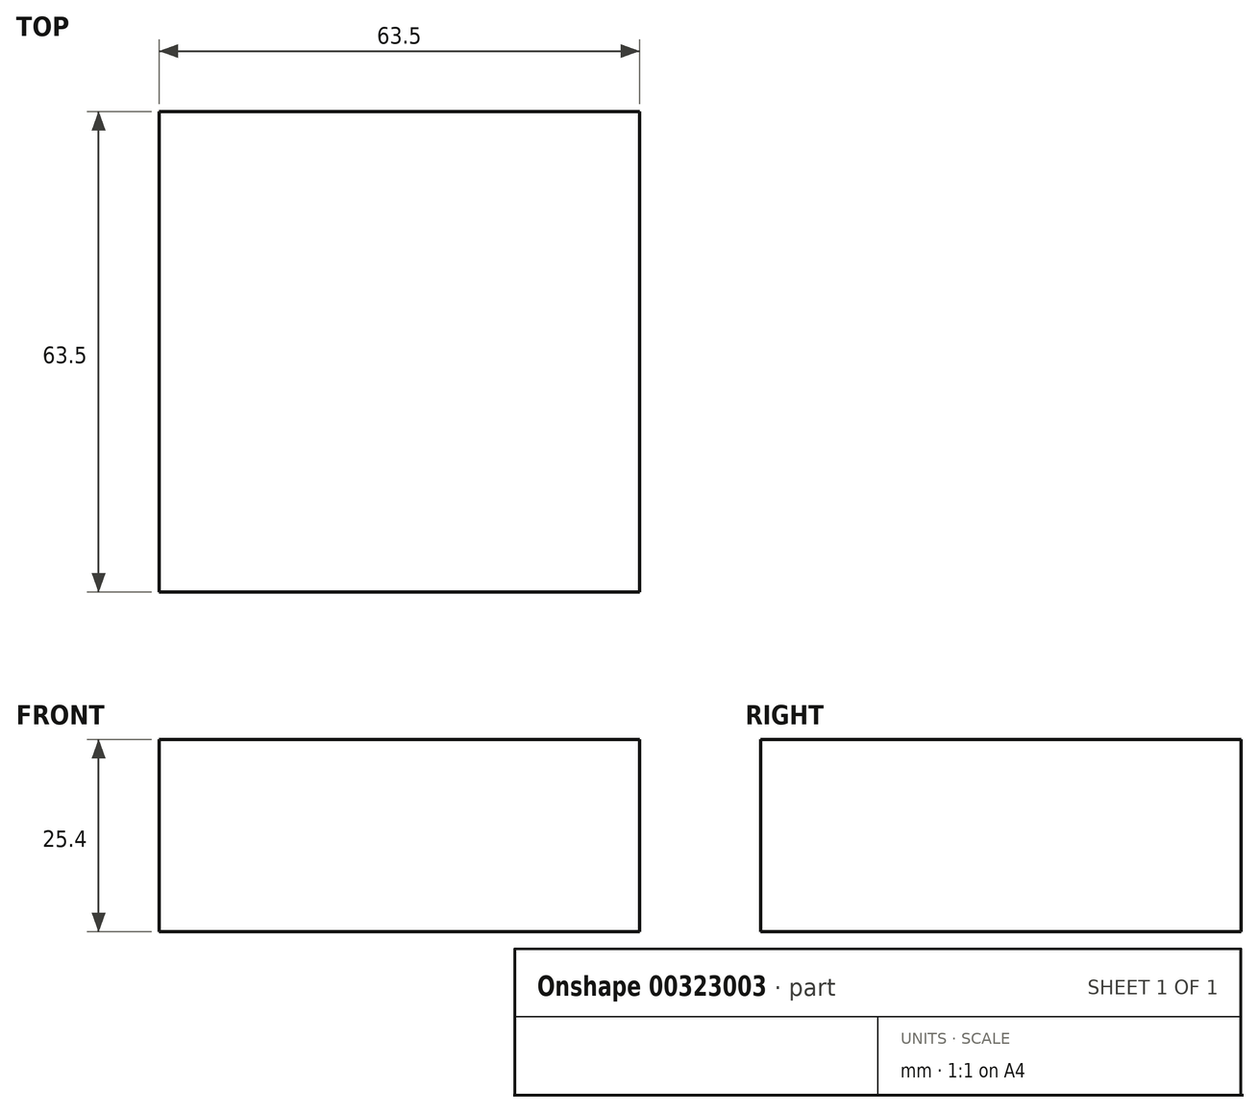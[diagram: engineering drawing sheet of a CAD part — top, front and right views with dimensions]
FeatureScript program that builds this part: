
annotation { "Feature Type Name" : "Feature", "Feature Type Description" : "" }
export const myFeature = defineFeature(function(context is Context, id is Id, definition is map)
    precondition{}
    {
        {
            var Q0;
            Q0=qCreatedBy(makeId("Top.planeOp"),FACE);
            var sketch = newSketch(context, id + "F0", { "sketchPlane" : qUnion([Q0])});
            skLineSegment(sketch, "E0.bottom", {"start": v(0, 0) * mm, "end": v(63.5, 0) * mm});
            skLineSegment(sketch, "E0.top", {"start": v(0, -63.5) * mm, "end": v(63.5, -63.5) * mm});
            skLineSegment(sketch, "E0.left", {"start": v(0, 0) * mm, "end": v(0, -63.5) * mm});
            skLineSegment(sketch, "E0.right", {"start": v(63.5, 0) * mm, "end": v(63.5, -63.5) * mm});
            skSolve(sketch);
        }
        {
            var Q0;
            Q0 = qSketchRegion(id + "F0", true);
            extrude(context, id + "F1", {"entities" : qUnion([Q0]), "depth" : 25.4 * mm});
        }
    });
